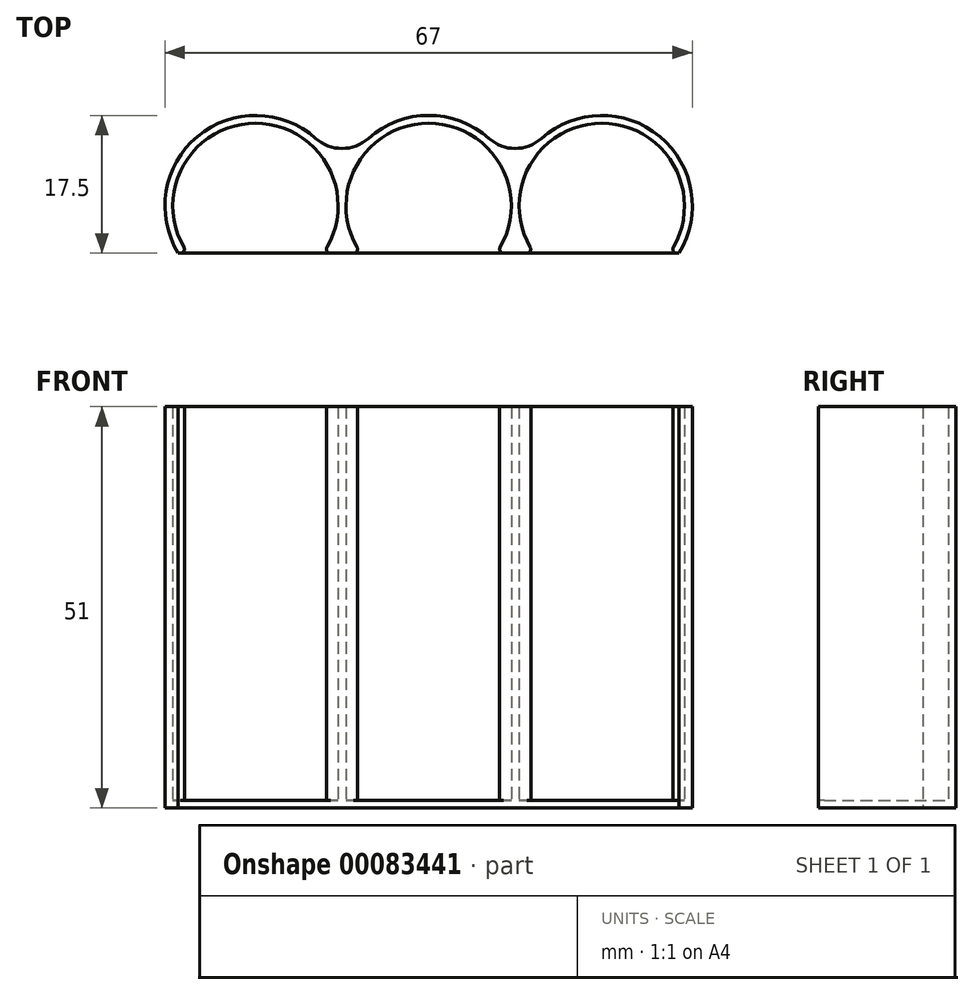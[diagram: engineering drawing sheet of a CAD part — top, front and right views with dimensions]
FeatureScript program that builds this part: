
annotation { "Feature Type Name" : "Feature", "Feature Type Description" : "" }
export const myFeature = defineFeature(function(context is Context, id is Id, definition is map)
    precondition{}
    {
        {
            var Q0;
            Q0=qCreatedBy(makeId("Top.planeOp"),FACE);
            var sketch = newSketch(context, id + "F0", { "sketchPlane" : qUnion([Q0])});
            skCircle(sketch, "E0", {"center": v(0, 0) * mm, "radius": 10.5 * mm});
            skCircle(sketch, "E1", {"center": v(0, 0) * mm, "radius": 11.5 * mm});
            skCircle(sketch, "E2.1.0.0", {"center": v(22, 0) * mm, "radius": 11.5 * mm});
            skCircle(sketch, "E2.1.0.1", {"center": v(22, 0) * mm, "radius": 10.5 * mm});
            skCircle(sketch, "E2.2.0.0", {"center": v(44, 0) * mm, "radius": 11.5 * mm});
            skCircle(sketch, "E2.2.0.1", {"center": v(44, 0) * mm, "radius": 10.5 * mm});
            skLineSegment(sketch, "E2.direction1", {"start": v(0, 0) * mm, "end": v(22, 0) * mm, "construction": true});
            skSolve(sketch);
        }
        {
            var Q0;
            Q0=makeQuery(id+"F0.imprint","IMPRINT",FACE,{"disambiguationData":[TD([[makeQuery(id+"F0.imprint","IMPRINT",EDGE,{"derivedFrom":sQuery(id+"F0.wireOp",EDGE,"E0")}),1.0]])]});
            var Q1;
            Q1=makeQuery(id+"F0.imprint","IMPRINT",FACE,{"disambiguationData":[TD([[makeQuery(id+"F0.imprint","IMPRINT",EDGE,{"derivedFrom":sQuery(id+"F0.wireOp",EDGE,"E2.1.0.1")}),1.0]])]});
            var Q2;
            Q2=makeQuery(id+"F0.imprint","IMPRINT",FACE,{"disambiguationData":[TD([[makeQuery(id+"F0.imprint","IMPRINT",EDGE,{"derivedFrom":sQuery(id+"F0.wireOp",EDGE,"E0")}),-1.0]])]});
            var Q3;
            {var subQ0=sQuery(id+"F0.wireOp",EDGE,"E2.1.0.0");var subQ1=sQuery(id+"F0.wireOp",EDGE,"E1");var subQ2=makeQuery(id+"F0.imprint","INTERSECT",VERTEX,{"disambiguationData":[OD(0.0)],"derivedFrom":[subQ1,subQ0]});Q3=makeQuery(id+"F0.imprint","IMPRINT",FACE,{"disambiguationData":[TD([[makeQuery(id+"F0.imprint","IMPRINT",EDGE,{"disambiguationData":[TD([[subQ2,1.0]])],"derivedFrom":subQ1}),1.0]])]});}
            var Q4;
            Q4=makeQuery(id+"F0.imprint","IMPRINT",FACE,{"disambiguationData":[TD([[makeQuery(id+"F0.imprint","IMPRINT",EDGE,{"derivedFrom":sQuery(id+"F0.wireOp",EDGE,"E2.1.0.1")}),-1.0]])]});
            var Q5;
            {var subQ0=sQuery(id+"F0.wireOp",EDGE,"E2.2.0.0");var subQ1=sQuery(id+"F0.wireOp",EDGE,"E2.1.0.0");var subQ2=makeQuery(id+"F0.imprint","INTERSECT",VERTEX,{"disambiguationData":[OD(0.0)],"derivedFrom":[subQ1,subQ0]});Q5=makeQuery(id+"F0.imprint","IMPRINT",FACE,{"disambiguationData":[TD([[makeQuery(id+"F0.imprint","IMPRINT",EDGE,{"disambiguationData":[TD([[subQ2,1.0]])],"derivedFrom":subQ1}),1.0]])]});}
            var Q6;
            Q6=makeQuery(id+"F0.imprint","IMPRINT",FACE,{"disambiguationData":[TD([[makeQuery(id+"F0.imprint","IMPRINT",EDGE,{"derivedFrom":sQuery(id+"F0.wireOp",EDGE,"E2.2.0.1")}),-1.0]])]});
            var Q7;
            Q7=makeQuery(id+"F0.imprint","IMPRINT",FACE,{"disambiguationData":[TD([[makeQuery(id+"F0.imprint","IMPRINT",EDGE,{"derivedFrom":sQuery(id+"F0.wireOp",EDGE,"E2.2.0.1")}),1.0]])]});
            extrude(context, id + "F1", {"entities" : qUnion([Q0, Q1, Q2, Q3, Q4, Q5, Q6, Q7]), "oppositeDirection" : true, "depth" : 1 * mm});
        }
        {
            var Q0;
            Q0=makeQuery(id+"F0.imprint","IMPRINT",FACE,{"disambiguationData":[TD([[makeQuery(id+"F0.imprint","IMPRINT",EDGE,{"derivedFrom":sQuery(id+"F0.wireOp",EDGE,"E0")}),-1.0]])]});
            var Q1;
            {var subQ0=sQuery(id+"F0.wireOp",EDGE,"E2.1.0.0");var subQ1=sQuery(id+"F0.wireOp",EDGE,"E1");var subQ2=makeQuery(id+"F0.imprint","INTERSECT",VERTEX,{"disambiguationData":[OD(0.0)],"derivedFrom":[subQ1,subQ0]});Q1=makeQuery(id+"F0.imprint","IMPRINT",FACE,{"disambiguationData":[TD([[makeQuery(id+"F0.imprint","IMPRINT",EDGE,{"disambiguationData":[TD([[subQ2,1.0]])],"derivedFrom":subQ1}),1.0]])]});}
            var Q2;
            Q2=makeQuery(id+"F0.imprint","IMPRINT",FACE,{"disambiguationData":[TD([[makeQuery(id+"F0.imprint","IMPRINT",EDGE,{"derivedFrom":sQuery(id+"F0.wireOp",EDGE,"E2.1.0.1")}),-1.0]])]});
            var Q3;
            {var subQ0=sQuery(id+"F0.wireOp",EDGE,"E2.2.0.0");var subQ1=sQuery(id+"F0.wireOp",EDGE,"E2.1.0.0");var subQ2=makeQuery(id+"F0.imprint","INTERSECT",VERTEX,{"disambiguationData":[OD(0.0)],"derivedFrom":[subQ1,subQ0]});Q3=makeQuery(id+"F0.imprint","IMPRINT",FACE,{"disambiguationData":[TD([[makeQuery(id+"F0.imprint","IMPRINT",EDGE,{"disambiguationData":[TD([[subQ2,1.0]])],"derivedFrom":subQ1}),1.0]])]});}
            var Q4;
            Q4=makeQuery(id+"F0.imprint","IMPRINT",FACE,{"disambiguationData":[TD([[makeQuery(id+"F0.imprint","IMPRINT",EDGE,{"derivedFrom":sQuery(id+"F0.wireOp",EDGE,"E2.2.0.1")}),-1.0]])]});
            extrude(context, id + "F2", {"entities" : qUnion([Q0, Q1, Q2, Q3, Q4]), "operationType" : NewBodyOperationType.ADD, "depth" : 50 * mm});
        }
        {
            var Q0;
            {var subQ0=sQuery(id+"F0.wireOp",EDGE,"E2.1.0.0");var subQ1=sQuery(id+"F0.wireOp",EDGE,"E1");var subQ2=makeQuery(id+"F0.imprint","INTERSECT",VERTEX,{"disambiguationData":[OD(0.0)],"derivedFrom":[subQ1,subQ0]});Q0=makeQuery(id+"F2.boolean.opBoolean","MERGE",EDGE,{"derivedFrom":[makeQuery(id+"F1.opExtrude","SWEPT_EDGE",EDGE,{"disambiguationData":[OSD([subQ1,subQ0]),TDD([subQ2])]}),makeQuery(id+"F2.opExtrude","SWEPT_EDGE",EDGE,{"disambiguationData":[OSD([subQ1,subQ0]),TDD([subQ2])]})]});}
            var Q1;
            {var subQ0=sQuery(id+"F0.wireOp",EDGE,"E2.2.0.0");var subQ1=sQuery(id+"F0.wireOp",EDGE,"E2.1.0.0");var subQ2=makeQuery(id+"F0.imprint","INTERSECT",VERTEX,{"disambiguationData":[OD(0.0)],"derivedFrom":[subQ1,subQ0]});Q1=makeQuery(id+"F2.boolean.opBoolean","MERGE",EDGE,{"derivedFrom":[makeQuery(id+"F1.opExtrude","SWEPT_EDGE",EDGE,{"disambiguationData":[OSD([subQ1,subQ0]),TDD([subQ2])]}),makeQuery(id+"F2.opExtrude","SWEPT_EDGE",EDGE,{"disambiguationData":[OSD([subQ1,subQ0]),TDD([subQ2])]})]});}
            var Q2;
            {var subQ0=sQuery(id+"F0.wireOp",EDGE,"E2.1.0.0");var subQ1=sQuery(id+"F0.wireOp",EDGE,"E1");var subQ2=makeQuery(id+"F0.imprint","INTERSECT",VERTEX,{"disambiguationData":[OD(1.0)],"derivedFrom":[subQ1,subQ0]});Q2=makeQuery(id+"F2.boolean.opBoolean","MERGE",EDGE,{"derivedFrom":[makeQuery(id+"F1.opExtrude","SWEPT_EDGE",EDGE,{"disambiguationData":[OSD([subQ1,subQ0]),TDD([subQ2])]}),makeQuery(id+"F2.opExtrude","SWEPT_EDGE",EDGE,{"disambiguationData":[OSD([subQ1,subQ0]),TDD([subQ2])]})]});}
            var Q3;
            {var subQ0=sQuery(id+"F0.wireOp",EDGE,"E2.2.0.0");var subQ1=sQuery(id+"F0.wireOp",EDGE,"E2.1.0.0");var subQ2=makeQuery(id+"F0.imprint","INTERSECT",VERTEX,{"disambiguationData":[OD(1.0)],"derivedFrom":[subQ1,subQ0]});Q3=makeQuery(id+"F2.boolean.opBoolean","MERGE",EDGE,{"derivedFrom":[makeQuery(id+"F1.opExtrude","SWEPT_EDGE",EDGE,{"disambiguationData":[OSD([subQ1,subQ0]),TDD([subQ2])]}),makeQuery(id+"F2.opExtrude","SWEPT_EDGE",EDGE,{"disambiguationData":[OSD([subQ1,subQ0]),TDD([subQ2])]})]});}
            fillet(context, id + "F3", {"entities" : qUnion([Q0, Q1, Q2, Q3]), "radius" : 5 * mm, "tangentPropagation" : true, "allowEdgeOverflow" : false});
        }
        {
            var Q0;
            Q0=makeQuery(id+"F2.opExtrude","CAP_FACE",FACE,{"disambiguationData":[OSD([sQuery(id+"F0.wireOp",EDGE,"E0"),sQuery(id+"F0.wireOp",EDGE,"E1"),sQuery(id+"F0.wireOp",EDGE,"E2.1.0.0"),sQuery(id+"F0.wireOp",EDGE,"E2.1.0.1"),sQuery(id+"F0.wireOp",EDGE,"E2.2.0.0"),sQuery(id+"F0.wireOp",EDGE,"E2.2.0.1")])],"isStart":false});
            var sketch = newSketch(context, id + "F4", { "sketchPlane" : qUnion([Q0])});
            skLineSegment(sketch, "E3.bottom", {"start": v(-13.28, -6) * mm, "end": v(55.25, -6) * mm});
            skLineSegment(sketch, "E3.top", {"start": v(-13.28, -16.08) * mm, "end": v(55.25, -16.08) * mm});
            skLineSegment(sketch, "E3.left", {"start": v(-13.28, -6) * mm, "end": v(-13.28, -16.08) * mm});
            skLineSegment(sketch, "E3.right", {"start": v(55.25, -6) * mm, "end": v(55.25, -16.08) * mm});
            skSolve(sketch);
        }
        {
            var Q0;
            {var subQ3=sQuery(id+"F0.wireOp",EDGE,"E2.1.0.0");var subQ4=sQuery(id+"F0.wireOp",EDGE,"E1");var subQ7=makeQuery(id+"F0.imprint","INTERSECT",VERTEX,{"disambiguationData":[OD(1.0)],"derivedFrom":[subQ4,subQ3]});Q0=makeQuery(id+"F4.imprint","IMPRINT",FACE,{"disambiguationData":[TD([[makeQuery(id+"F4.imprint","IMPRINT",EDGE,{"derivedFrom":makeQuery(id+"F2.opExtrude","CAP_EDGE",EDGE,{"disambiguationData":[OSD([subQ3]),TDD([makeQuery(id+"F0.imprint","IMPRINT",EDGE,{"disambiguationData":[TD([[subQ7,-1.0]])],"derivedFrom":subQ3})])],"isStart":false})}),1.0]])]});}
            var Q1;
            {var subQ0=sQuery(id+"F4.wireOp",EDGE,"E3.bottom");var subQ1=makeQuery(id+"F2.opExtrude","CAP_EDGE",EDGE,{"disambiguationData":[OSD([sQuery(id+"F0.wireOp",EDGE,"E0")])],"isStart":false});var subQ2=makeQuery(id+"F4.imprint","INTERSECT",VERTEX,{"disambiguationData":[OD(0.0)],"derivedFrom":[subQ1,subQ0]});Q1=makeQuery(id+"F4.imprint","IMPRINT",FACE,{"disambiguationData":[TD([[makeQuery(id+"F4.imprint","IMPRINT",EDGE,{"disambiguationData":[TD([[subQ2,-1.0]])],"derivedFrom":subQ0}),-1.0]])]});}
            var Q2;
            {var subQ0=sQuery(id+"F4.wireOp",EDGE,"E3.bottom");var subQ1=makeQuery(id+"F2.opExtrude","CAP_EDGE",EDGE,{"disambiguationData":[OSD([sQuery(id+"F0.wireOp",EDGE,"E2.1.0.1")])],"isStart":false});var subQ2=makeQuery(id+"F4.imprint","INTERSECT",VERTEX,{"disambiguationData":[OD(0.0)],"derivedFrom":[subQ1,subQ0]});Q2=makeQuery(id+"F4.imprint","IMPRINT",FACE,{"disambiguationData":[TD([[makeQuery(id+"F4.imprint","IMPRINT",EDGE,{"disambiguationData":[TD([[subQ2,-1.0]])],"derivedFrom":subQ0}),-1.0]])]});}
            var Q3;
            {var subQ0=sQuery(id+"F4.wireOp",EDGE,"E3.bottom");var subQ1=makeQuery(id+"F2.opExtrude","CAP_EDGE",EDGE,{"disambiguationData":[OSD([sQuery(id+"F0.wireOp",EDGE,"E2.2.0.1")])],"isStart":false});var subQ2=makeQuery(id+"F4.imprint","INTERSECT",VERTEX,{"disambiguationData":[OD(0.0)],"derivedFrom":[subQ1,subQ0]});Q3=makeQuery(id+"F4.imprint","IMPRINT",FACE,{"disambiguationData":[TD([[makeQuery(id+"F4.imprint","IMPRINT",EDGE,{"disambiguationData":[TD([[subQ2,-1.0]])],"derivedFrom":subQ0}),-1.0]])]});}
            var Q4;
            Q4=makeQuery(id+"F1.opExtrude","CAP_FACE",FACE,{"disambiguationData":[OSD([sQuery(id+"F0.wireOp",EDGE,"E1"),sQuery(id+"F0.wireOp",EDGE,"E2.1.0.0"),sQuery(id+"F0.wireOp",EDGE,"E2.2.0.0")])],"isStart":false});
            extrude(context, id + "F5", {"entities" : qUnion([Q0, Q1, Q2, Q3]), "operationType" : NewBodyOperationType.REMOVE, "endBound" : BoundingType.UP_TO_SURFACE, "oppositeDirection" : true, "endBoundEntityFace" : qUnion([Q4]), "depth" : 25 * mm});
        }
        {
            var Q0;
            Q0=makeQuery(id+"F5.boolean.opBoolean","INTERSECT",EDGE,{"disambiguationData":[OD(0.0)],"derivedFrom":[makeQuery(id+"F2.opExtrude","SWEPT_FACE",FACE,{"disambiguationData":[OSD([sQuery(id+"F0.wireOp",EDGE,"E0")])]}),makeQuery(id+"F5.opExtrude","SWEPT_FACE",FACE,{"disambiguationData":[OSD([sQuery(id+"F4.wireOp",EDGE,"E3.bottom")])]})]});
            var Q1;
            Q1=makeQuery(id+"F5.boolean.opBoolean","INTERSECT",EDGE,{"disambiguationData":[OD(1.0)],"derivedFrom":[makeQuery(id+"F2.opExtrude","SWEPT_FACE",FACE,{"disambiguationData":[OSD([sQuery(id+"F0.wireOp",EDGE,"E0")])]}),makeQuery(id+"F5.opExtrude","SWEPT_FACE",FACE,{"disambiguationData":[OSD([sQuery(id+"F4.wireOp",EDGE,"E3.bottom")])]})]});
            var Q2;
            Q2=makeQuery(id+"F5.boolean.opBoolean","INTERSECT",EDGE,{"disambiguationData":[OD(0.0)],"derivedFrom":[makeQuery(id+"F2.opExtrude","SWEPT_FACE",FACE,{"disambiguationData":[OSD([sQuery(id+"F0.wireOp",EDGE,"E2.1.0.1")])]}),makeQuery(id+"F5.opExtrude","SWEPT_FACE",FACE,{"disambiguationData":[OSD([sQuery(id+"F4.wireOp",EDGE,"E3.bottom")])]})]});
            var Q3;
            Q3=makeQuery(id+"F5.boolean.opBoolean","INTERSECT",EDGE,{"disambiguationData":[OD(1.0)],"derivedFrom":[makeQuery(id+"F2.opExtrude","SWEPT_FACE",FACE,{"disambiguationData":[OSD([sQuery(id+"F0.wireOp",EDGE,"E2.1.0.1")])]}),makeQuery(id+"F5.opExtrude","SWEPT_FACE",FACE,{"disambiguationData":[OSD([sQuery(id+"F4.wireOp",EDGE,"E3.bottom")])]})]});
            var Q4;
            Q4=makeQuery(id+"F5.boolean.opBoolean","INTERSECT",EDGE,{"disambiguationData":[OD(1.0)],"derivedFrom":[makeQuery(id+"F2.opExtrude","SWEPT_FACE",FACE,{"disambiguationData":[OSD([sQuery(id+"F0.wireOp",EDGE,"E2.2.0.1")])]}),makeQuery(id+"F5.opExtrude","SWEPT_FACE",FACE,{"disambiguationData":[OSD([sQuery(id+"F4.wireOp",EDGE,"E3.bottom")])]})]});
            var Q5;
            Q5=makeQuery(id+"F5.boolean.opBoolean","INTERSECT",EDGE,{"disambiguationData":[OD(0.0)],"derivedFrom":[makeQuery(id+"F2.opExtrude","SWEPT_FACE",FACE,{"disambiguationData":[OSD([sQuery(id+"F0.wireOp",EDGE,"E2.2.0.1")])]}),makeQuery(id+"F5.opExtrude","SWEPT_FACE",FACE,{"disambiguationData":[OSD([sQuery(id+"F4.wireOp",EDGE,"E3.bottom")])]})]});
            fillet(context, id + "F6", {"entities" : qUnion([Q0, Q1, Q2, Q3, Q4, Q5]), "radius" : .5 * mm, "tangentPropagation" : true, "allowEdgeOverflow" : false});
        }
    });
